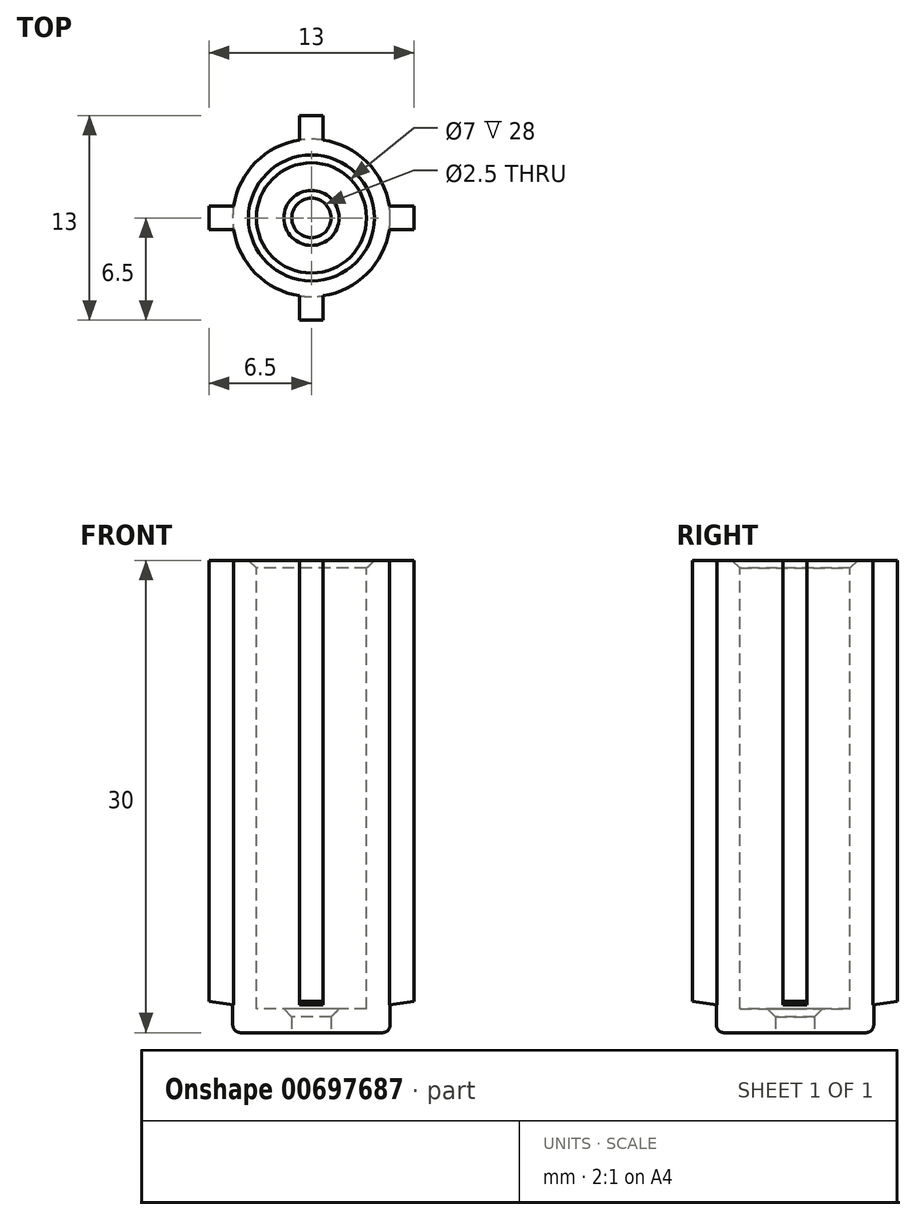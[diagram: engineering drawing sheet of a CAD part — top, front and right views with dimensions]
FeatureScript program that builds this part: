
annotation { "Feature Type Name" : "Feature", "Feature Type Description" : "" }
export const myFeature = defineFeature(function(context is Context, id is Id, definition is map)
    precondition{}
    {
        {
            var Q0;
            Q0=qCreatedBy(makeId("Top.planeOp"),FACE);
            cPlane(context, id + "F0", {"entities" : qUnion([Q0]), "cplaneType" : CPlaneType.OFFSET, "offset" : 0 * mm, "width" : 150 * mm, "height" : 150 * mm});
        }
        {
            var Q0;
            Q0=qCreatedBy(id+"F0.planeOp",FACE);
            var sketch = newSketch(context, id + "F1", { "sketchPlane" : qUnion([Q0])});
            skCircle(sketch, "E0", {"center": v(-25, 25) * mm, "radius": 5 * mm});
            skCircle(sketch, "E1", {"center": v(-25, 25) * mm, "radius": 3.5 * mm});
            skCircle(sketch, "E2", {"center": v(-25, 25) * mm, "radius": 2.5 * mm, "construction": true});
            skSolve(sketch);
        }
        {
            var Q0;
            Q0=qSketchRegion(id+"F1",true);
            extrude(context, id + "F2", {"entities" : qUnion([Q0]), "oppositeDirection" : true, "depth" : 30 * mm, "offsetDistance" : 25 * mm});
        }
        {
            var Q0;
            Q0=makeQuery(id+"F2.opExtrude","CAP_FACE",FACE,{"disambiguationData":[OSD([sQuery(id+"F1.wireOp",EDGE,"E0"),sQuery(id+"F1.wireOp",EDGE,"E1")])],"isStart":true});
            cPlane(context, id + "F3", {"entities" : qUnion([Q0]), "cplaneType" : CPlaneType.OFFSET, "offset" : 0 * mm, "width" : 150 * mm, "height" : 150 * mm});
        }
        {
            var Q0;
            Q0=qCreatedBy(id+"F3.planeOp",FACE);
            var sketch = newSketch(context, id + "F4", { "sketchPlane" : qUnion([Q0])});
            skCircle(sketch, "E3.0", {"center": v(-25, 25) * mm, "radius": 3.5 * mm, "construction": true});
            skLineSegment(sketch, "E4.bottom", {"start": v(-25.75, 31.5) * mm, "end": v(-24.25, 31.5) * mm});
            skLineSegment(sketch, "E4.top", {"start": v(-25.75, 28.86) * mm, "end": v(-24.25, 28.86) * mm});
            skLineSegment(sketch, "E4.left", {"start": v(-25.75, 31.5) * mm, "end": v(-25.75, 28.86) * mm});
            skLineSegment(sketch, "E4.right", {"start": v(-24.25, 31.5) * mm, "end": v(-24.25, 28.86) * mm});
            skPoint(sketch, "E5.center", {"position": v(0, 0) * mm});
            skSolve(sketch);
        }
        {
            var Q0;
            Q0=qSketchRegion(id+"F4",true);
            extrude(context, id + "F5", {"entities" : qUnion([Q0]), "operationType" : NewBodyOperationType.ADD, "oppositeDirection" : true, "depth" : (30 - 0.5) * mm, "offsetDistance" : 25 * mm});
        }
        {
            var Q0;
            Q0=makeQuery(id+"F2.opExtrude","SWEPT_BODY",BODY,{"disambiguationData":[OSD([sQuery(id+"F1.wireOp",EDGE,"E0"),sQuery(id+"F1.wireOp",EDGE,"E1")])]});
            var Q1;
            Q1=makeQuery(id+"F2.opExtrude","SWEPT_FACE",FACE,{"disambiguationData":[OSD([sQuery(id+"F1.wireOp",EDGE,"E1")])]});
            circularPattern(context, id + "F6", {"operationType" : NewBodyOperationType.ADD, "entities" : qUnion([Q0]), "axis" : qUnion([Q1]), "angle" : 360 * degree, "instanceCount" : 4, "equalSpace" : true});
        }
        {
            var Q0;
            {var subQ0=makeQuery(id+"F5.boolean.opBoolean","MERGE",FACE,{"derivedFrom":[makeQuery(id+"F2.opExtrude","CAP_FACE",FACE,{"disambiguationData":[OSD([sQuery(id+"F1.wireOp",EDGE,"E0"),sQuery(id+"F1.wireOp",EDGE,"E1")])],"isStart":true}),makeQuery(id+"F5.opExtrude","CAP_FACE",FACE,{"disambiguationData":[OSD([sQuery(id+"F4.wireOp",EDGE,"E4.bottom"),sQuery(id+"F4.wireOp",EDGE,"E4.top"),sQuery(id+"F4.wireOp",EDGE,"E4.left"),sQuery(id+"F4.wireOp",EDGE,"E4.right")])],"isStart":true})]});Q0=makeQuery(id+"F6.boolean.opBoolean","MERGE",FACE,{"derivedFrom":[subQ0,makeQuery(id+"F6.opPattern","COPY",FACE,{"derivedFrom":subQ0,"instanceName":"1"}),makeQuery(id+"F6.opPattern","COPY",FACE,{"derivedFrom":subQ0,"instanceName":"2"}),makeQuery(id+"F6.opPattern","COPY",FACE,{"derivedFrom":subQ0,"instanceName":"3"})]});}
            cPlane(context, id + "F7", {"entities" : qUnion([Q0]), "cplaneType" : CPlaneType.OFFSET, "offset" : 30 * mm, "oppositeDirection" : true, "width" : 150 * mm, "height" : 150 * mm});
        }
        {
            var Q0;
            Q0=qCreatedBy(id+"F7.planeOp",FACE);
            var sketch = newSketch(context, id + "F8", { "sketchPlane" : qUnion([Q0])});
            skCircle(sketch, "E6.0", {"center": v(-25, 25) * mm, "radius": 3.5 * mm});
            skCircle(sketch, "E7", {"center": v(-25, 25) * mm, "radius": 1.25 * mm});
            skSolve(sketch);
        }
        {
            var Q0;
            Q0=qSketchRegion(id+"F8",true);
            extrude(context, id + "F9", {"entities" : qUnion([Q0]), "operationType" : NewBodyOperationType.ADD, "depth" : 1.5 * mm, "offsetDistance" : 25 * mm});
        }
        {
            var Q0;
            Q0=makeQuery(id+"F6.opPattern","COPY",EDGE,{"derivedFrom":makeQuery(id+"F5.opExtrude","CAP_EDGE",EDGE,{"disambiguationData":[OSD([sQuery(id+"F4.wireOp",EDGE,"E4.bottom")])],"isStart":false}),"instanceName":"1"});
            var Q1;
            Q1=makeQuery(id+"F5.opExtrude","CAP_EDGE",EDGE,{"disambiguationData":[OSD([sQuery(id+"F4.wireOp",EDGE,"E4.bottom")])],"isStart":false});
            var Q2;
            Q2=makeQuery(id+"F6.opPattern","COPY",EDGE,{"derivedFrom":makeQuery(id+"F5.opExtrude","CAP_EDGE",EDGE,{"disambiguationData":[OSD([sQuery(id+"F4.wireOp",EDGE,"E4.bottom")])],"isStart":false}),"instanceName":"3"});
            var Q3;
            Q3=makeQuery(id+"F6.opPattern","COPY",EDGE,{"derivedFrom":makeQuery(id+"F5.opExtrude","CAP_EDGE",EDGE,{"disambiguationData":[OSD([sQuery(id+"F4.wireOp",EDGE,"E4.bottom")])],"isStart":false}),"instanceName":"2"});
            chamfer(context, id + "F10", {"entities" : qUnion([Q0, Q1, Q2, Q3]), "chamferType" : ChamferType.TWO_OFFSETS, "width1" : 1.5 * mm, "oppositeDirection" : false, "width2" : 10 * mm, "tangentPropagation" : true});
        }
        {
            var Q0;
            Q0=makeQuery(id+"F2.opExtrude","CAP_EDGE",EDGE,{"disambiguationData":[OSD([sQuery(id+"F1.wireOp",EDGE,"E1")])],"isStart":true});
            var Q1;
            Q1=makeQuery(id+"F9.opExtrude","CAP_EDGE",EDGE,{"disambiguationData":[OSD([sQuery(id+"F8.wireOp",EDGE,"E7")])],"isStart":false});
            chamfer(context, id + "F11", {"entities" : qUnion([Q0, Q1]), "width" : 0.5 * mm, "tangentPropagation" : true});
        }
        {
            var Q0;
            Q0=makeQuery(id+"F2.opExtrude","CAP_EDGE",EDGE,{"disambiguationData":[OSD([sQuery(id+"F1.wireOp",EDGE,"E0")])],"isStart":false});
            fillet(context, id + "F12", {"entities" : qUnion([Q0]), "radius" : 0.5 * mm, "tangentPropagation" : true, "allowEdgeOverflow" : false});
        }
    });
